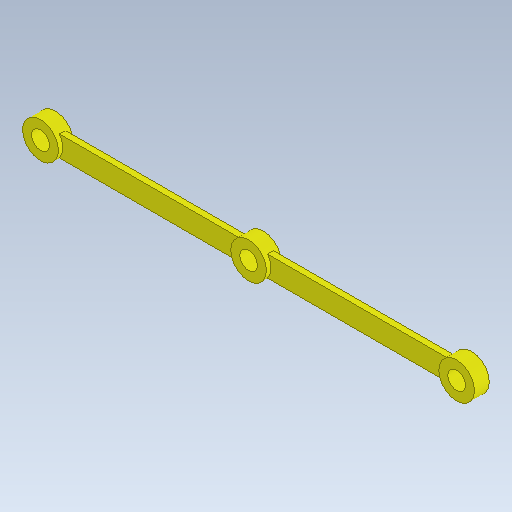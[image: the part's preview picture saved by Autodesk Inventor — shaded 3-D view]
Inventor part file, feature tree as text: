
AUTODESK INVENTOR PART (.ipt)
format: ipt  version: 2020.5 (Build 245400000, 400)  size: 131,072 bytes
history: native  units: mm
features: extrude x4, sketch x4, projected_geometry x2, mirror x1
ambient origin geometry x8: Origin, YZ Plane, XZ Plane, XY Plane, X Axis, Y Axis, Z Axis, Center Point
bodies: Solid1 (feature_tree)
feature tree (11):
  extrude  "Extrusion1"  Depth=6.0mm
  extrude  "Extrusion2"  Depth=7.0mm
  mirror  "Mirror1"
  extrude  "Extrusion3"  Depth=1.5mm TaperAngle=0.0deg
  extrude  "Extrusion4"  Depth=5.0mm TaperAngle=0.0deg
  sketch  "Sketch1"  dims[d0=140.0mm d1=6.0mm]
  sketch  "Sketch2"  dims[d2=12.0mm d3=7.0mm]
  sketch  "Sketch3"  dims[d4=5.0mm d5=0.0mm d6=1.5mm d7=0.0mm]
  projected_geometry  "Projected Loop1"
  sketch  "Sketch4"  dims[d8=12.0mm d9=5.0mm d10=0.0mm d11=6.0mm d12=5.0mm d13=0.0mm]
  projected_geometry  "Projected Loop2"
